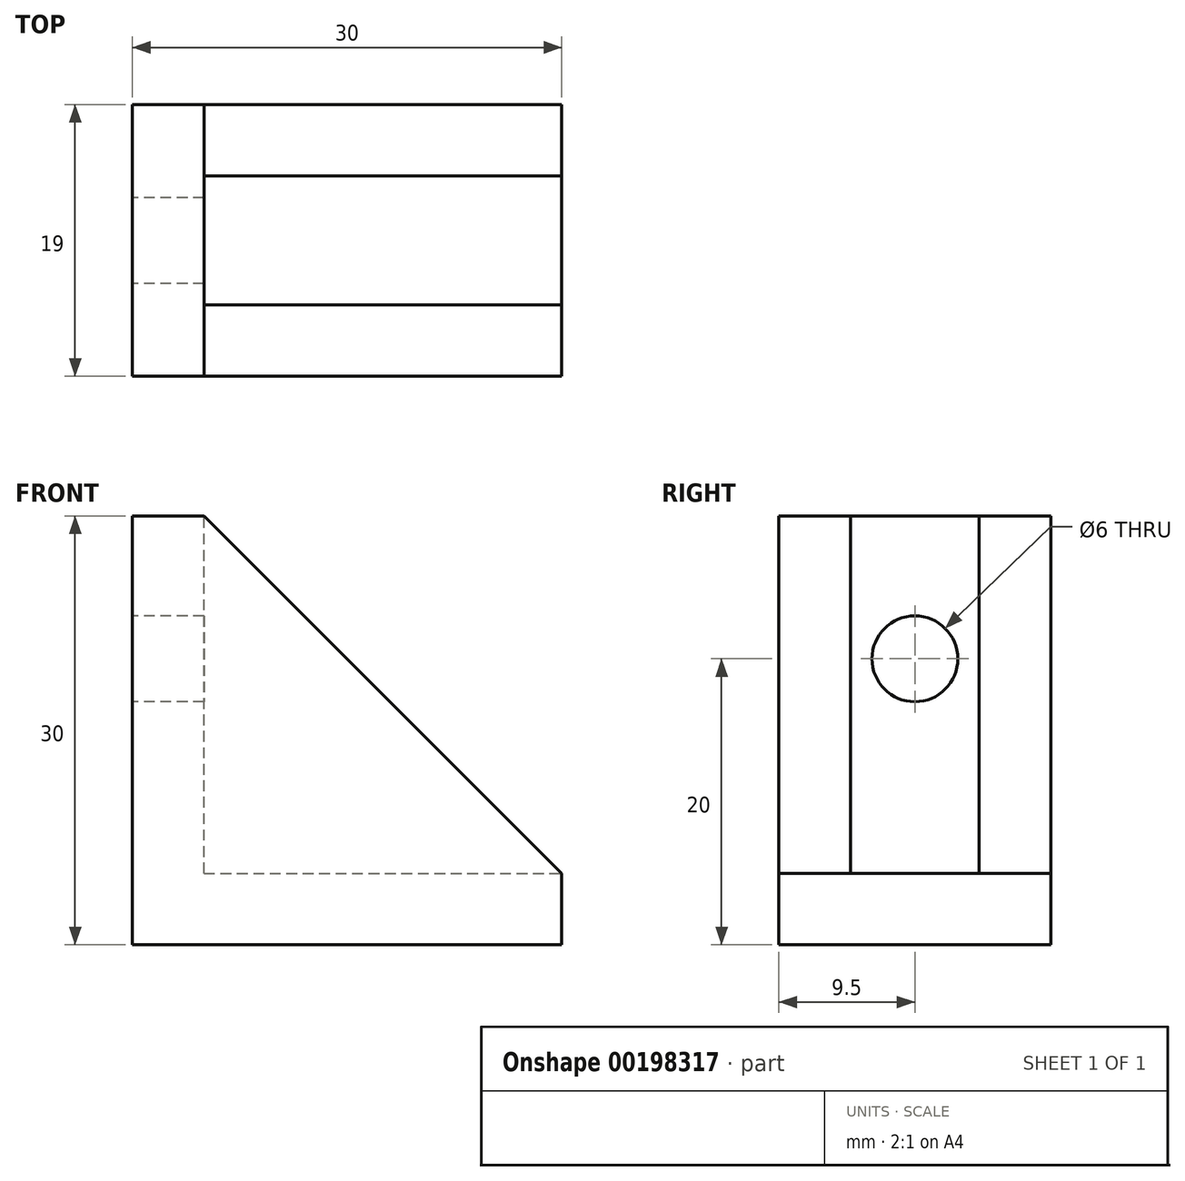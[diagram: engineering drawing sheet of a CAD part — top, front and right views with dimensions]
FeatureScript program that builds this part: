
annotation { "Feature Type Name" : "Feature", "Feature Type Description" : "" }
export const myFeature = defineFeature(function(context is Context, id is Id, definition is map)
    precondition{}
    {
        {
            var Q0;
            Q0=qCreatedBy(makeId("Front.planeOp"),FACE);
            var sketch = newSketch(context, id + "F0", { "sketchPlane" : qUnion([Q0])});
            skLineSegment(sketch, "E0", {"start": v(0, 0) * mm, "end": v(0, 30) * mm});
            skLineSegment(sketch, "E1", {"start": v(0, 30) * mm, "end": v(5, 30) * mm});
            skLineSegment(sketch, "E2", {"start": v(0, 0) * mm, "end": v(30, 0) * mm});
            skLineSegment(sketch, "E3", {"start": v(30, 0) * mm, "end": v(30, 5) * mm});
            skLineSegment(sketch, "E4", {"start": v(30, 5) * mm, "end": v(5, 30) * mm});
            skSolve(sketch);
        }
        {
            var Q0;
            Q0=makeQuery(id+"F0.imprint","IMPRINT",FACE,{"disambiguationData":[TD([[makeQuery(id+"F0.imprint","IMPRINT",EDGE,{"derivedFrom":sQuery(id+"F0.wireOp",EDGE,"E0")}),-1.0]])]});
            extrude(context, id + "F1", {"entities" : qUnion([Q0]), "oppositeDirection" : true, "depth" : 19 * mm});
        }
        {
            var Q0;
            Q0=qCreatedBy(makeId("Top.planeOp"),FACE);
            cPlane(context, id + "F2", {"entities" : qUnion([Q0]), "cplaneType" : CPlaneType.OFFSET, "offset" : 30 * mm, "width" : 150 * mm, "height" : 150 * mm});
        }
        {
            var Q0;
            Q0=qCreatedBy(id+"F2.planeOp",FACE);
            var sketch = newSketch(context, id + "F3", { "sketchPlane" : qUnion([Q0])});
            skLineSegment(sketch, "E5.bottom", {"start": v(5, 14) * mm, "end": v(30, 14) * mm});
            skLineSegment(sketch, "E5.top", {"start": v(5, 5) * mm, "end": v(30, 5) * mm});
            skLineSegment(sketch, "E5.left", {"start": v(5, 14) * mm, "end": v(5, 5) * mm});
            skLineSegment(sketch, "E5.right", {"start": v(30, 14) * mm, "end": v(30, 5) * mm});
            skSolve(sketch);
        }
        {
            var Q0;
            Q0 = qSketchRegion(id + "F3", true);
            extrude(context, id + "F4", {"entities" : qUnion([Q0]), "operationType" : NewBodyOperationType.REMOVE, "oppositeDirection" : true, "depth" : 25 * mm});
        }
        {
            var Q0;
            Q0=makeQuery(id+"F1.opExtrude","SWEPT_FACE",FACE,{"disambiguationData":[OSD([sQuery(id+"F0.wireOp",EDGE,"E0")])]});
            var sketch = newSketch(context, id + "F5", { "sketchPlane" : qUnion([Q0])});
            skLineSegment(sketch, "E6", {"start": v(-9.5, 30) * mm, "end": v(-9.5, 20) * mm, "construction": true});
            skCircle(sketch, "E7", {"center": v(-9.5, 20) * mm, "radius": 3 * mm});
            skCircle(sketch, "E8", {"center": v(-9.5, 20) * mm, "radius": 5 * mm});
            skLineSegment(sketch, "E9", {"start": v(-9.5, 15) * mm, "end": v(-7, 15) * mm, "construction": true});
            skLineSegment(sketch, "E10", {"start": v(-7, 15) * mm, "end": v(-7, 0) * mm, "construction": true});
            skLineSegment(sketch, "E11", {"start": v(-7, 0) * mm, "end": v(-12, 0) * mm, "construction": true});
            skLineSegment(sketch, "E12", {"start": v(-12, 0) * mm, "end": v(-12, 15) * mm, "construction": true});
            skLineSegment(sketch, "E13", {"start": v(-12, 15) * mm, "end": v(-9.5, 15) * mm, "construction": true});
            skSolve(sketch);
        }
        {
            var Q0;
            Q0=makeQuery(id+"F5.imprint","IMPRINT",FACE,{"disambiguationData":[TD([[makeQuery(id+"F5.imprint","IMPRINT",EDGE,{"derivedFrom":sQuery(id+"F5.wireOp",EDGE,"E7")}),1.0]])]});
            var Q1;
            Q1=makeQuery(id+"F4.boolean.opBoolean","COPY",FACE,{"derivedFrom":makeQuery(id+"F4.opExtrude","SWEPT_FACE",FACE,{"disambiguationData":[OSD([sQuery(id+"F3.wireOp",EDGE,"E5.left")])]})});
            extrude(context, id + "F6", {"entities" : qUnion([Q0]), "operationType" : NewBodyOperationType.REMOVE, "endBound" : BoundingType.UP_TO_SURFACE, "oppositeDirection" : true, "endBoundEntityFace" : qUnion([Q1]), "depth" : 25 * mm});
        }
    });
